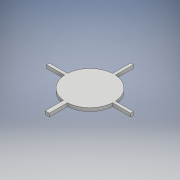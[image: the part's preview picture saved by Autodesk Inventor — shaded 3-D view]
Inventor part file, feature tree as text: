
AUTODESK INVENTOR PART (.ipt)
format: ipt  version: 2018 (Build 220112000, 112)  size: 131,072 bytes
history: native  units: mm
features: other x1, extrude x1, sketch x1
ambient origin geometry x8: Origin, YZ Plane, XZ Plane, XY Plane, X Axis, Y Axis, Z Axis, Center Point
bodies: Body1 (feature_tree)
feature tree (3):
  other  "Bryła1"
  extrude  "Wyciągnięcie proste1"  Depth=87.0mm
  sketch  "Szkic1"
